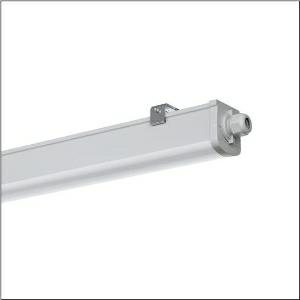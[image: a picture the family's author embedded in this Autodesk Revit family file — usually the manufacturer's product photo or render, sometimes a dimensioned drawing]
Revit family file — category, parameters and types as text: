
# Revit family: monsun_r__31_51fa20dk450b_5819
name_source: partatom
category: Lighting Fixtures
units: mm (PartAtom-declared; Revit-internal decimal feet)

## family parameters
Cut with Voids When Loaded = No
Host = Face
Light Source = No
Part Type = Normal
Room Calculation Point = No
Round Connector Dimension = Use Diameter
Shared = No

## types (1)
- Monsun® 31 (1 x LED, 5100 lm, 38 W, 4000K)
    Apparent Load = 38 VA
    CIE Flux Codes = 42 72 91 92 100
    Color Rendering = 80
    Color Temperature = 4000K
    Default Elevation = 1800 mm
    Description = Monsun® 31, damp-proof luminaire, primary optical cover: diffuser, of PC, frosted, light emission: direct distribution, primary light characteristic: symmetric, installation type: surface-mounted, LED, rated luminous flux: 5.100lm, luminous efficacy: 134lm/W, light colour: 840, colour temperature: 4000K, control gear: DALI 2, with terminal, 5+1-pole, max. 2.5mm², through-wiring: 3x 2.5mm² + 3x 1.5mm², mains connection: 220..240V, AC, 50/60Hz, rated input power: 38W, housing, luminaire housing, of PC, light grey (RAL 7035), length: 1.158mm, width: 68mm, height: 76mm, protection rating (complete): IP66, insulation class (complete): insulation class II (safety insulation), certification: CE, ENEC, UKCA, protection symbol: D, impact resistance: IK08, permissible operating ambient temperature: -20..+40°C, corresponds to IFS (International Featured Standards) requirements for safety and quality in the food industry, contact your sales advisor before using the luminaires in applications with unclear chemical exposure, large temperature fluctuations or condensation-forming humidity, packaging unit: 1 piece
    Height = 77 mm
    Lamp = 1 x LED
    Lamp Light Flux = 5100 lm
    Lamp Power = 38 W
    Lamp count = 1
    Length = 1218 mm
    Luminous efficacy = 134 lm/W
    Manufacturer = Siteco
    ModVariant = No
    Model = 51FA20DK450B
    Mounting Place = Ceiling
    Mounting Type = Surface mounted
    Number of Poles = 1
    OnlyDefault = Yes
    Power Factor = 1
    Product Name = Monsun® 31
    Product group = damp-proof luminaire
    ProductGroupID = 300
    Protection Class = Protection class II
    Protection Degree = IP 66
    RLX_Detail_Level = 1
    RLX_Emergency_Light_Flux = 0 lm
    RLX_Emergency_Type = 0
    RLX_Emergency_Type_DB = No
    RlxData = <blob elided: 33029 chars, md5=b308c310>
    Socket = socket
    Standby Power = 0 W
    System Light Flux = 5100 lm
    System Power = 38 W
    Type Comments = Product without accessories
    Type Image = l_1006174.jpg
    URL = http://relux.com
    VarID = ---
    Voltage = 0 V
    Weight = 0.00 kg
    Width = 69 mm

## geometry (parser evidence)
native form markers: Blend x4, Sweep x13
no freeform markers — native parametric forms only
